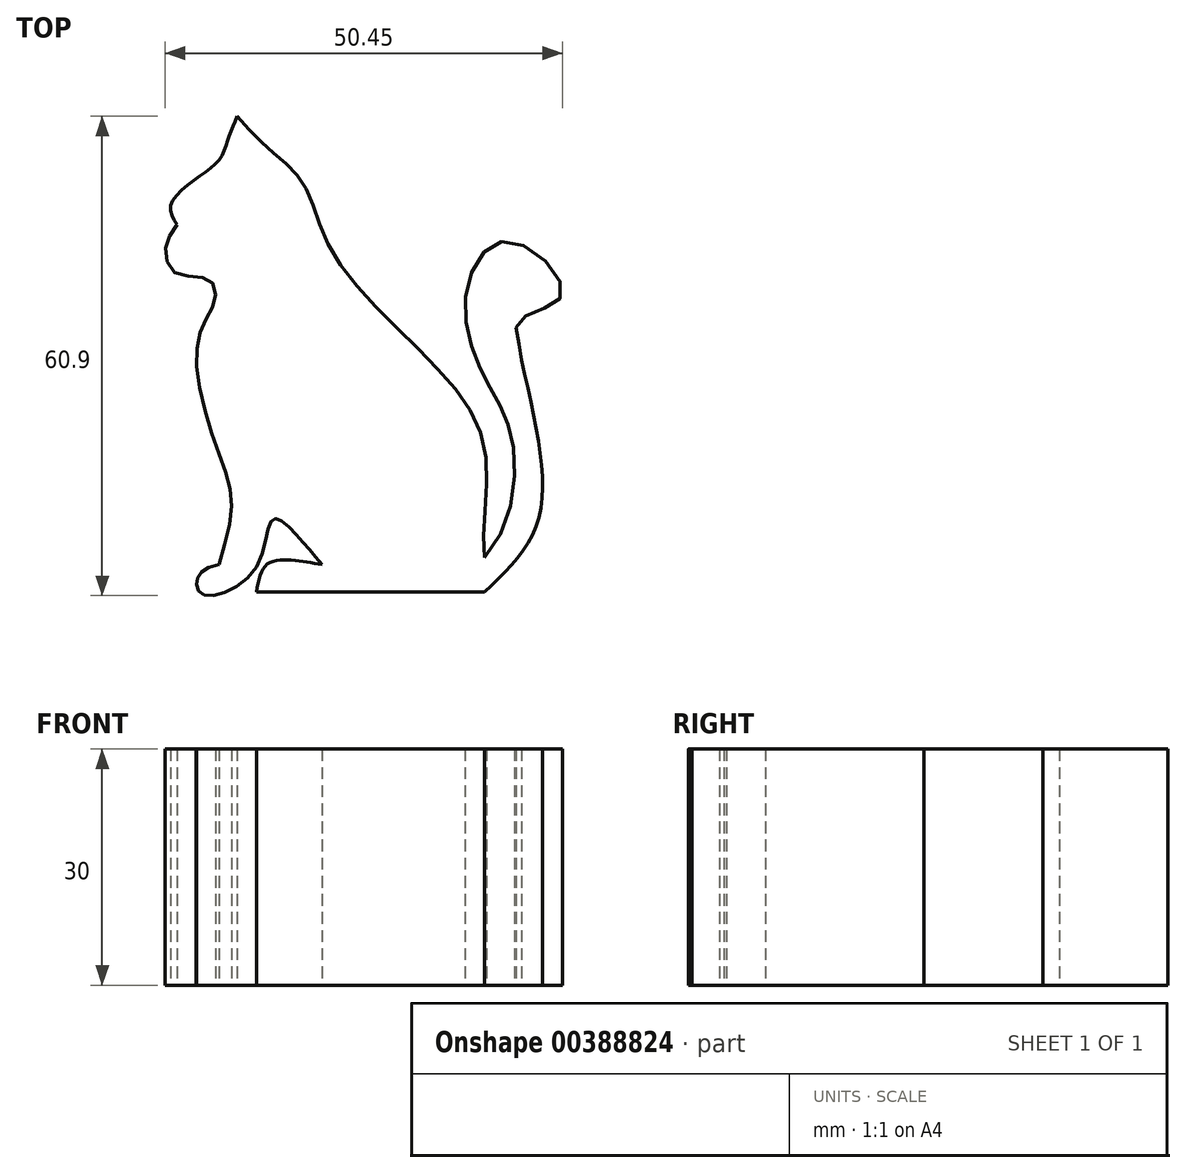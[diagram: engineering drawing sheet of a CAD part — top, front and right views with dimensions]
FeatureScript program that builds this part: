
annotation { "Feature Type Name" : "Feature", "Feature Type Description" : "" }
export const myFeature = defineFeature(function(context is Context, id is Id, definition is map)
    precondition{}
    {
        {
            var Q0;
            Q0=qCreatedBy(makeId("Top.planeOp"),FACE);
            var sketch = newSketch(context, id + "F0", { "sketchPlane" : qUnion([Q0])});
            skFitSpline(sketch, "E0", {"points": [v(-16.25, 28.08) * mm, v(-17.28, 25.44) * mm, v(-18.3, 22.83) * mm, v(-21.32, 20.22) * mm, v(-24.66, 16.7) * mm, v(-23.86, 14.32) * mm], "startDerivative": vector(-4.53, -15.63) * mm, "endDerivative": vector(7.79, -13.16) * mm});
            skFitSpline(sketch, "E1", {"points": [v(-23.86, 14.32) * mm, v(-25.34, 11.14) * mm, v(-23.86, 8.08) * mm, v(-19.89, 7.4) * mm, v(-18.98, 5.01) * mm, v(-20.57, 1.5) * mm, v(-21.32, -4.18) * mm, v(-18.64, -14.51) * mm, v(-16.92, -20.97) * mm, v(-18.54, -28.89) * mm], "startDerivative": vector(-22.72, -32.56) * mm, "endDerivative": vector(-17.37, -59.67) * mm});
            skFitSpline(sketch, "E2", {"points": [v(-18.54, -28.89) * mm, v(-21.32, -30.87) * mm, v(-20.44, -32.7) * mm, v(-13.92, -29.4) * mm, v(-11.65, -23.1) * mm, v(-8.86, -24.93) * mm, v(-5.42, -28.89) * mm], "startDerivative": vector(-33.65, -5.6) * mm, "endDerivative": vector(19.28, -22) * mm});
            skFitSpline(sketch, "E3", {"points": [v(-5.42, -28.89) * mm, v(-9.38, -28.3) * mm, v(-12.45, -28.89) * mm, v(-13.77, -32.35) * mm], "startDerivative": vector(-11.38, 2.1) * mm, "endDerivative": vector(-2.17, -13.07) * mm});
            skLineSegment(sketch, "E4", {"start": v(-13.77, -32.35) * mm, "end": v(15.21, -32.35) * mm});
            skFitSpline(sketch, "E5", {"points": [v(15.21, -32.35) * mm, v(22.1, -22.97) * mm, v(19.9, -2.87) * mm], "startDerivative": vector(20.54, 19.55) * mm, "endDerivative": vector(-9.29, 42.02) * mm});
            skFitSpline(sketch, "E6", {"points": [v(19.9, -2.87) * mm, v(19.48, 1.94) * mm, v(25.01, 5.32) * mm, v(18.44, 12.19) * mm, v(12.88, 5.76) * mm, v(15.21, -5.09) * mm, v(18.74, -13.09) * mm, v(15.21, -27.95) * mm], "startDerivative": vector(5.65, 40.5) * mm, "endDerivative": vector(-56.7, -56.35) * mm});
            skFitSpline(sketch, "E7", {"points": [v(15.21, -27.95) * mm, v(15.21, -14.11) * mm, v(7.16, -1.86) * mm, v(-4.28, 11.02) * mm, v(-7.64, 19.24) * mm, v(-11.54, 23.4) * mm, v(-16.25, 28.08) * mm], "startDerivative": vector(-9.23, 55.55) * mm, "endDerivative": vector(-36.66, 42.71) * mm});
            skSolve(sketch);
        }
        {
            var Q0;
            Q0 = qSketchRegion(id + "F0", true);
            extrude(context, id + "F1", {"entities" : qUnion([Q0]), "depth" : 30 * mm});
        }
    });
